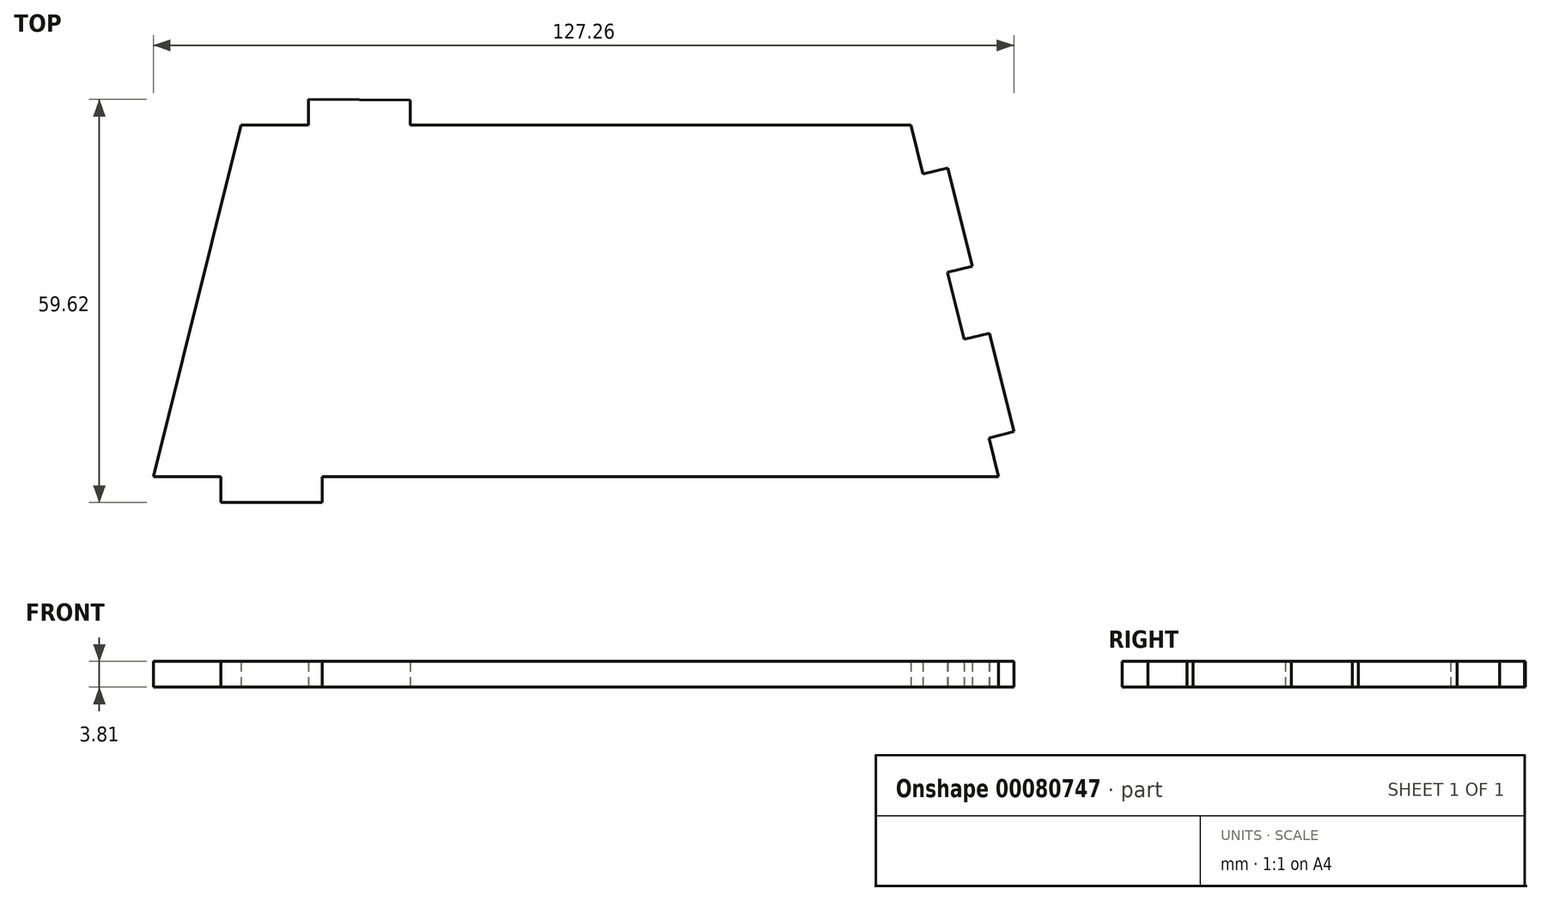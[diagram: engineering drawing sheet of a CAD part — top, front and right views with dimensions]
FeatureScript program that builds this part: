
annotation { "Feature Type Name" : "Feature", "Feature Type Description" : "" }
export const myFeature = defineFeature(function(context is Context, id is Id, definition is map)
    precondition{}
    {
        {
            var Q0;
            Q0=qCreatedBy(makeId("Top.planeOp"),FACE);
            var sketch = newSketch(context, id + "F0", { "sketchPlane" : qUnion([Q0])});
            skLineSegment(sketch, "E0.top", {"start": v(62.5, -26) * mm, "end": v(-62.5, -26) * mm});
            skLineSegment(sketch, "E0.left", {"start": v(62.5, 26) * mm, "end": v(62.5, -26) * mm});
            skPoint(sketch, "E0.middle", {"position": v(0, 0) * mm});
            skLineSegment(sketch, "E1", {"start": v(-62.5, 0) * mm, "end": v(0, 0) * mm, "construction": true});
            skLineSegment(sketch, "E2", {"start": v(-52.5, -26) * mm, "end": v(-52.5, -29.8) * mm});
            skLineSegment(sketch, "E3", {"start": v(-52.5, -29.8) * mm, "end": v(-37.5, -29.8) * mm});
            skLineSegment(sketch, "E4", {"start": v(-37.5, -29.8) * mm, "end": v(-37.5, -26) * mm});
            skLineSegment(sketch, "E5", {"start": v(62.5, 26) * mm, "end": v(-49.53, 26) * mm});
            skLineSegment(sketch, "E6", {"start": v(-49.53, 26) * mm, "end": v(-62.5, -26) * mm});
            skLineSegment(sketch, "E7", {"start": v(49.5, 26) * mm, "end": v(62.5, -26) * mm});
            skLineSegment(sketch, "E8", {"start": v(55, 19.7) * mm, "end": v(51.3, 18.78) * mm});
            skLineSegment(sketch, "E9", {"start": v(55, 19.7) * mm, "end": v(58.64, 5.15) * mm});
            skLineSegment(sketch, "E10", {"start": v(54.94, 4.23) * mm, "end": v(58.64, 5.15) * mm});
            skLineSegment(sketch, "E11", {"start": v(61.12, -4.76) * mm, "end": v(57.42, -5.69) * mm});
            skLineSegment(sketch, "E12", {"start": v(61.12, -4.76) * mm, "end": v(64.76, -19.31) * mm});
            skLineSegment(sketch, "E13", {"start": v(61.06, -20.24) * mm, "end": v(64.76, -19.31) * mm});
            skLineSegment(sketch, "E14", {"start": v(-39.53, 26) * mm, "end": v(-39.53, 29.81) * mm});
            skLineSegment(sketch, "E15", {"start": v(-39.53, 29.81) * mm, "end": v(-24.54, 29.73) * mm});
            skLineSegment(sketch, "E16", {"start": v(-24.54, 29.73) * mm, "end": v(-24.54, 26) * mm});
            skSolve(sketch);
        }
        {
            var Q0;
            Q0=makeQuery(id+"F0.imprint","IMPRINT",FACE,{"disambiguationData":[TD([[makeQuery(id+"F0.imprint","IMPRINT",EDGE,{"derivedFrom":sQuery(id+"F0.wireOp",EDGE,"E0.bottom")}),1.0]])]});
            var Q1;
            {var subQ0=sQuery(id+"F0.wireOp",EDGE,"d6c4e1d5-604d-4cb2-8208-546e49f99e940.MirrorCS");Q1=makeQuery(id+"F0.imprint","IMPRINT",FACE,{"disambiguationData":[TD([[makeQuery(id+"F0.imprint","IMPRINT",EDGE,{"derivedFrom":subQ0}),-1.0]])]});}
            var Q2;
            {var subQ0=sQuery(id+"F0.wireOp",EDGE,"E2");Q2=makeQuery(id+"F0.imprint","IMPRINT",FACE,{"disambiguationData":[TD([[makeQuery(id+"F0.imprint","IMPRINT",EDGE,{"derivedFrom":subQ0}),1.0]])]});}
            var Q3;
            {var subQ0=sQuery(id+"F0.wireOp",EDGE,"E6");Q3=makeQuery(id+"F0.imprint","IMPRINT",FACE,{"disambiguationData":[TD([[makeQuery(id+"F0.imprint","IMPRINT",EDGE,{"derivedFrom":subQ0}),1.0]])]});}
            var Q4;
            {var subQ2=sQuery(id+"F0.wireOp",EDGE,"FzK2Zswt-UR5U-boKB-zPHS-QaINhW8Eak5i");Q4=makeQuery(id+"F0.imprint","IMPRINT",FACE,{"disambiguationData":[TD([[makeQuery(id+"F0.imprint","IMPRINT",EDGE,{"derivedFrom":subQ2}),-1.0]])]});}
            var Q5;
            {var subQ0=sQuery(id+"F0.wireOp",EDGE,"E11");Q5=makeQuery(id+"F0.imprint","IMPRINT",FACE,{"disambiguationData":[TD([[makeQuery(id+"F0.imprint","IMPRINT",EDGE,{"derivedFrom":subQ0}),1.0]])]});}
            var Q6;
            {var subQ0=sQuery(id+"F0.wireOp",EDGE,"E8");Q6=makeQuery(id+"F0.imprint","IMPRINT",FACE,{"disambiguationData":[TD([[makeQuery(id+"F0.imprint","IMPRINT",EDGE,{"derivedFrom":subQ0}),1.0]])]});}
            var Q7;
            {var subQ0=sQuery(id+"F0.wireOp",EDGE,"E12");var subQ1=sQuery(id+"F0.wireOp",EDGE,"E0.left");var subQ2=makeQuery(id+"F0.imprint","INTERSECT",VERTEX,{"derivedFrom":[subQ1,subQ0]});Q7=makeQuery(id+"F0.imprint","IMPRINT",FACE,{"disambiguationData":[TD([[makeQuery(id+"F0.imprint","IMPRINT",EDGE,{"disambiguationData":[TD([[subQ2,-1.0]])],"derivedFrom":subQ1}),1.0]])]});}
            var Q8;
            {var subQ0=sQuery(id+"F0.wireOp",EDGE,"E14");Q8=makeQuery(id+"F0.imprint","IMPRINT",FACE,{"disambiguationData":[TD([[makeQuery(id+"F0.imprint","IMPRINT",EDGE,{"derivedFrom":subQ0}),-1.0]])]});}
            extrude(context, id + "F1", {"entities" : qUnion([Q0, Q1, Q2, Q3, Q4, Q5, Q6, Q7, Q8]), "depth" : 3.8 * mm});
        }
    });
